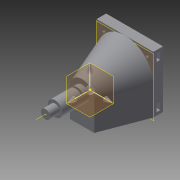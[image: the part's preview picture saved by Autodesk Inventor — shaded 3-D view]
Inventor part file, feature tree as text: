
AUTODESK INVENTOR PART (.ipt)
format: ipt  version: 2015 (Build 190159000, 159)  size: 240,640 bytes
history: native  units: in
note: dims shown in document units (in); Inventor stores cm internally (conversion verified against a paired STEP export)
features: sketch x10, extrude x9, other x4, mirror x1, plane x1, loft x1, revolve x1
ambient origin geometry x8: Origin, YZ Plane, XZ Plane, XY Plane, X Axis, Y Axis, Z Axis, Center Point
bodies: Solid1 (feature_tree)
feature tree (27):
  other  "Curvature1"
  extrude  "Extrusion1"  Depth=2.1654in TaperAngle=0.0deg
  extrude  "Extrusion2"  Depth=0.0787in
  extrude  "Extrusion3"  Depth=1.1142in
  sketch  "Sketch10"  dims[d24=0.2953in d25=0.1378in]
  extrude  "Extrusion5"  Depth=0.0787in
  extrude  "Extrusion4"  Depth=0.1969in
  mirror  "Mirror1"
  plane  "Work Plane1"
  extrude  "Extrusion6"  Depth=0.1378in
  loft  "Loft2"
  extrude  "Extrusion7"  Depth=0.2756in
  extrude  "Extrusion8"  Depth=0.1378in
  other  "Work Axis1"
  revolve  "Revolution1"  [1 undecoded]
  extrude  "Extrusion10"  TaperAngle=0.0deg  [1 undecoded]
  sketch  "Sketch2"  dims[d0=2.3425in d1=2.1654in d2=0.0in]
  sketch  "Sketch3"  dims[d3=0.6102in d5=0.0787in]
  sketch  "Sketch4"  dims[d6=1.1142in d7=0.0in d8=0.374in]
  sketch  "Sketch7"  dims[d9=0.3937in d10=0.0in d16=0.0787in]
  sketch  "Sketch9"  dims[d17=0.5315in d18=0.1969in]
  sketch  "Sketch11"  dims[d26=0.1181in d27=0.3937in d28=0.0in]
  other  "Edges2"
  other  "Edges3"
  sketch  "Sketch12"  dims[d29=0.2756in d30=0.2756in]
  sketch  "Sketch15"  dims[d34=0.3937in d36=0.0in d37=0.0in d38=0.0in d39=90.0deg d40=0.0in d41=90.0deg d42=1.2598in d43=0.0in d44=0.2362in d45=0.0in d46=0.0in d47=0.8661in d49=0.1969in d54=0.1969in d55=0.7874in d56=180.0deg d57=1.0in d58=0.0in]
  sketch  "Sketch14"  dims[d31=0.3937in d32=0.0in d33=0.1378in]
note: 2 required parameter values undecoded (feature->parameter linkage not recoverable at this tier; creation-order binding heuristic only, values carry confidence <= 0.55)